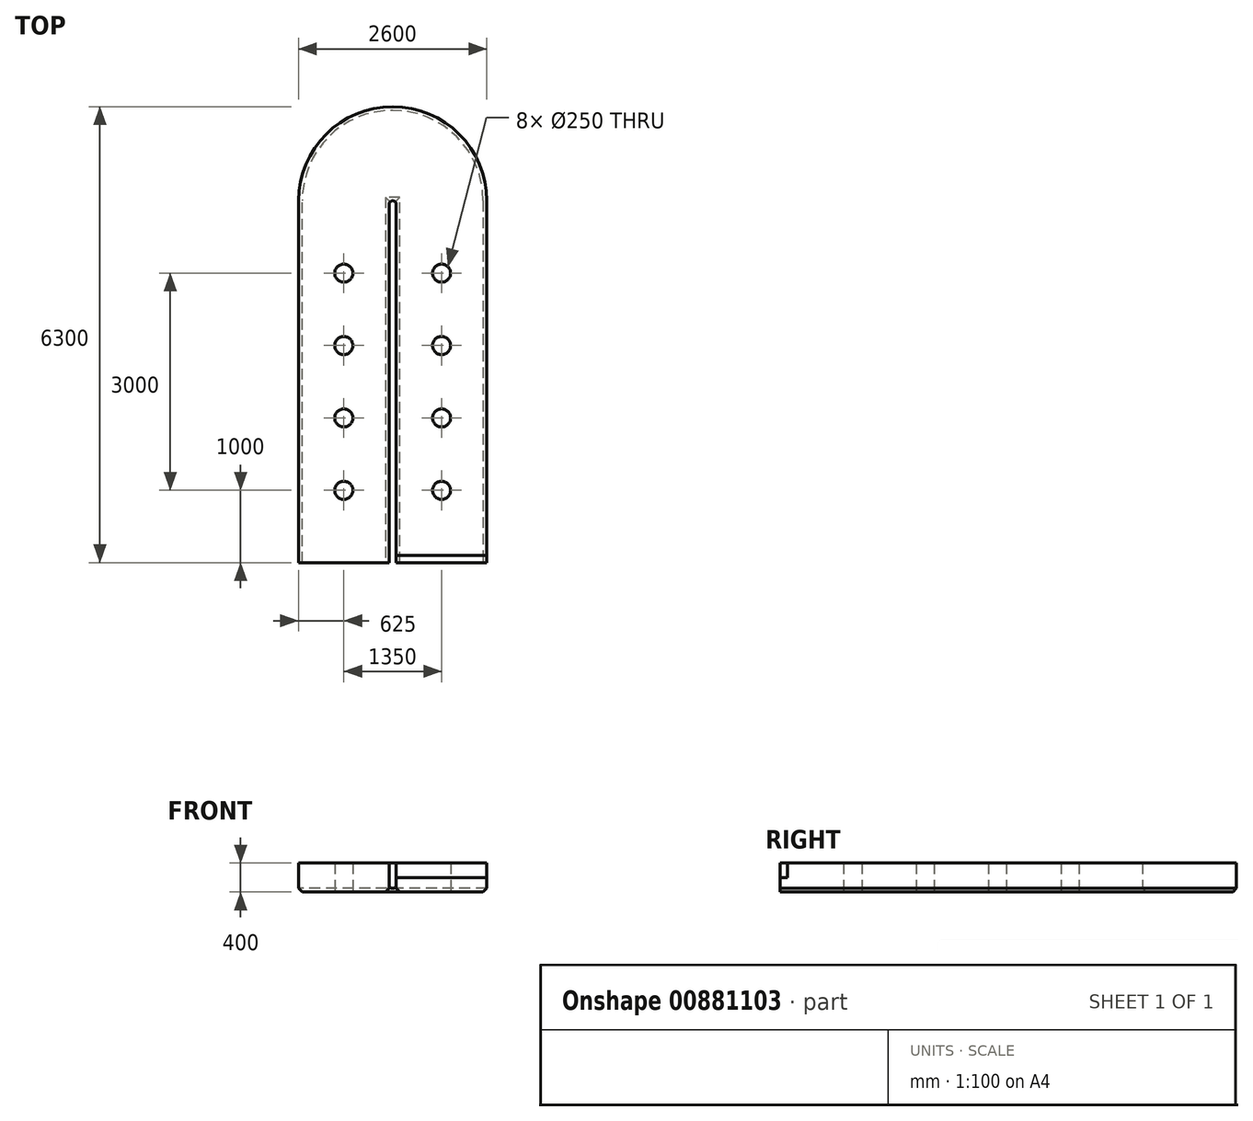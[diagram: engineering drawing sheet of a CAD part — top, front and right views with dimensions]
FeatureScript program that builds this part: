
annotation { "Feature Type Name" : "Feature", "Feature Type Description" : "" }
export const myFeature = defineFeature(function(context is Context, id is Id, definition is map)
    precondition{}
    {
        {
            var Q0;
            Q0=qCreatedBy(makeId("Top.planeOp"),FACE);
            var sketch = newSketch(context, id + "F0", { "sketchPlane" : qUnion([Q0])});
            skLineSegment(sketch, "E0", {"start": v(0, 0) * mm, "end": v(50, 0) * mm});
            skLineSegment(sketch, "E1", {"start": v(50, 0) * mm, "end": v(50, -5000) * mm});
            skLineSegment(sketch, "E2", {"start": v(0, 0) * mm, "end": v(-50, 0) * mm});
            skLineSegment(sketch, "E3", {"start": v(-50, 0) * mm, "end": v(-50, -5000) * mm});
            skLineSegment(sketch, "E4", {"start": v(50, -5000) * mm, "end": v(1300, -5000) * mm});
            skLineSegment(sketch, "E5", {"start": v(1300, -5000) * mm, "end": v(1300, 0) * mm});
            skLineSegment(sketch, "E6", {"start": v(-50, -5000) * mm, "end": v(-1300, -5000) * mm});
            skLineSegment(sketch, "E7", {"start": v(-1300, -5000) * mm, "end": v(-1300, 0) * mm});
            skArc(sketch, "E8", {"start": v(-1300, 0) * mm, "mid": v(0, 1300) * mm, "end": v(1300, 0) * mm});
            skLineSegment(sketch, "E9", {"start": v(0, 0) * mm, "end": v(0, -5000) * mm, "construction": true});
            skCircle(sketch, "E10", {"center": v(675, -1000) * mm, "radius": 125 * mm});
            skCircle(sketch, "E11.MirrorC", {"center": v(-675, -1000) * mm, "radius": 125 * mm});
            skCircle(sketch, "E12", {"center": v(675, -2000) * mm, "radius": 125 * mm});
            skCircle(sketch, "E13", {"center": v(675, -3000) * mm, "radius": 125 * mm});
            skCircle(sketch, "E14", {"center": v(675, -4000) * mm, "radius": 125 * mm});
            skCircle(sketch, "E15.MirrorC", {"center": v(-675, -2000) * mm, "radius": 125 * mm});
            skCircle(sketch, "E16.MirrorC", {"center": v(-675, -3000) * mm, "radius": 125 * mm});
            skCircle(sketch, "E17.MirrorC", {"center": v(-675, -4000) * mm, "radius": 125 * mm});
            skLineSegment(sketch, "E18", {"start": v(50, -4900) * mm, "end": v(1300, -4900) * mm});
            skSolve(sketch);
        }
        {
            var Q0;
            {var subQ3=sQuery(id+"F0.wireOp",EDGE,"E0");Q0=makeQuery(id+"F0.imprint","IMPRINT",FACE,{"disambiguationData":[TD([[makeQuery(id+"F0.imprint","IMPRINT",EDGE,{"derivedFrom":subQ3}),1.0]])]});}
            extrude(context, id + "F1", {"entities" : qUnion([Q0]), "depth" : 400 * mm, "offsetDistance" : 25 * mm});
        }
        {
            var Q0;
            {var subQ0=sQuery(id+"F0.wireOp",EDGE,"E4");Q0=makeQuery(id+"F0.imprint","IMPRINT",FACE,{"disambiguationData":[TD([[makeQuery(id+"F0.imprint","IMPRINT",EDGE,{"derivedFrom":subQ0}),1.0]])]});}
            extrude(context, id + "F2", {"entities" : qUnion([Q0]), "operationType" : NewBodyOperationType.ADD, "depth" : 200 * mm, "offsetDistance" : 25 * mm});
        }
        {
            var Q0;
            Q0=makeQuery(id+"F1.opExtrude","CAP_EDGE",EDGE,{"disambiguationData":[OSD([sQuery(id+"F0.wireOp",EDGE,"E7")])],"isStart":true});
            var Q1;
            Q1=makeQuery(id+"F1.opExtrude","CAP_EDGE",EDGE,{"disambiguationData":[OSD([sQuery(id+"F0.wireOp",EDGE,"E8")])],"isStart":true});
            var Q2;
            {var subQ0=sQuery(id+"F0.wireOp",EDGE,"E5");Q2=makeQuery(id+"F2.boolean.opBoolean","MERGE",EDGE,{"derivedFrom":[makeQuery(id+"F1.opExtrude","CAP_EDGE",EDGE,{"disambiguationData":[OSD([subQ0])],"isStart":true}),makeQuery(id+"F2.opExtrude","CAP_EDGE",EDGE,{"disambiguationData":[OSD([subQ0])],"isStart":true})]});}
            var Q3;
            Q3=makeQuery(id+"F1.opExtrude","CAP_EDGE",EDGE,{"disambiguationData":[OSD([sQuery(id+"F0.wireOp",EDGE,"E3")])],"isStart":true});
            var Q4;
            {var subQ0=sQuery(id+"F0.wireOp",EDGE,"E1");Q4=makeQuery(id+"F2.boolean.opBoolean","MERGE",EDGE,{"derivedFrom":[makeQuery(id+"F1.opExtrude","CAP_EDGE",EDGE,{"disambiguationData":[OSD([subQ0])],"isStart":true}),makeQuery(id+"F2.opExtrude","CAP_EDGE",EDGE,{"disambiguationData":[OSD([subQ0])],"isStart":true})]});}
            var Q5;
            Q5=makeQuery(id+"F1.opExtrude","CAP_EDGE",EDGE,{"disambiguationData":[OSD([sQuery(id+"F0.wireOp",EDGE,"E0"),sQuery(id+"F0.wireOp",EDGE,"E2")])],"isStart":true});
            chamfer(context, id + "F3", {"entities" : qUnion([Q0, Q1, Q2, Q3, Q4, Q5]), "width" : 50 * mm, "tangentPropagation" : true});
        }
        {
            var Q0;
            Q0=makeQuery(id+"F1.opExtrude","SWEPT_EDGE",EDGE,{"disambiguationData":[OSD([sQuery(id+"F0.wireOp",EDGE,"E0"),sQuery(id+"F0.wireOp",EDGE,"E1")])]});
            var Q1;
            Q1=makeQuery(id+"F1.opExtrude","SWEPT_EDGE",EDGE,{"disambiguationData":[OSD([sQuery(id+"F0.wireOp",EDGE,"E2"),sQuery(id+"F0.wireOp",EDGE,"E3")])]});
            fillet(context, id + "F4", {"entities" : qUnion([Q0, Q1]), "radius" : 50 * mm, "tangentPropagation" : true, "allowEdgeOverflow" : false});
        }
    });
